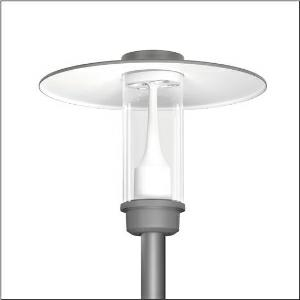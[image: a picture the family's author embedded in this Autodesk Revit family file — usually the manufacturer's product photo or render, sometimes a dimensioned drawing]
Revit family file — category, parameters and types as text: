
# Revit family: litepole_2_iq___p1_0a_5xa5425nf14hp_e36f
name_source: partatom
category: Lighting Fixtures
units: mm (PartAtom-declared; Revit-internal decimal feet)

## family parameters
Cut with Voids When Loaded = No
Host = Face
Light Source = No
Part Type = Normal
Room Calculation Point = No
Round Connector Dimension = Use Diameter
Shared = No

## types (1)
- --- (1 x LED, 4240 lm, 33.6 W, 2700K)
    Apparent Load = 34 VA
    CIE Flux Codes = 32 62 90 96 100
    Color Rendering = 70
    Color Temperature = 2700K
    Default Elevation = 1800 mm
    Description = Litepole 2 iQ, mast luminaire, Module 540 iQ-SR, primary light control with 3 zone facetted reflector, of plastic, silver coated, highly specular, structured, primary optical cover: cover, of PMMA, transparent, light distribution: P1.0a, light emission: direct distribution, primary light characteristic: strongly asymmetric, installation type: post-top, LED, High Power LED, rated luminous flux: 4.240lm, luminous efficacy: 126lm/W, light colour: 727, colour temperature: 2700K, control gear: iQ Street-Remote, control: pre-setting: logarithmic dimming characteristic, Street-Remote, Auto-Match, Temp-Guard, Lumen-Switch, Night-Set, Smart-Wire, Light-Fading, Desk-Remote (wireless, voltage-free reading and setting of iQ features in the workshop via application-optimized NFC function/RFID function), optimised constant luminous flux control (CLO 2.0), with terminal, 6-pole, max. 2.5mm², mains connection: 230..240V, AC, 50/60Hz, start of lifetime: 34W, end of service life: 36W, reduction: 15W, luminaire housing, upper part, of aluminium, coated, Siteco® metallic grey (DB 702S), diameter: 750mm, height: 590mm, spigot size: d x l = 76 x 70mm (post-top) | with reducer (optional accessory) 60 x 70mm, mounting height: 3..5m, post-top mast mounting element, of diecast aluminium, coated, Siteco® metallic grey (DB 702S), Module 540 iQ-SR, traffic white (RAL 9016), equipment: Power, protection rating (complete): IP65, insulation class (complete): insulation class II (safety insulation), certification: CE, ENEC, VDE, packaging unit: 1 piece

Light Distribution: P1.0a
    Height = 590 mm
    Lamp = 1 x LED
    Lamp Light Flux = 4240 lm
    Lamp Power = 33.6 W
    Lamp count = 1
    Length = 750 mm
    Luminous efficacy = 126 lm/W
    Manufacturer = Siteco
    ModVariant = No
    Model = 5XA5425NF14HP
    Number of Poles = 1
    OnlyDefault = Yes
    Power Factor = 1
    Product Name = Litepole 2 iQ | P1.0a
    Product group = mast luminaire | pylon top
    ProductGroupID = 6100
    Protection Class = Protection class II
    Protection Degree = IP 65
    RLX_Detail_Level = 1
    RLX_Emergency_Light_Flux = 0 lm
    RLX_Emergency_Type = 0
    RLX_Emergency_Type_DB = No
    RlxData = <blob elided: 32061 chars, md5=822b5c19>
    Socket = socket
    Standby Power = 0 W
    System Light Flux = 4240 lm
    System Power = 34 W
    Type Comments = factory setting: luminous flux: 100 % | dim-lin: 254 | 695 mA
    Type Image = l_1006518.jpg
    URL = http://relux.com
    VarID = @adj_152402
    Voltage = 0 V
    Weight = 0.00 kg
    Width = 0 mm  [stored 0 ft]

note: [stored X ft] marks values corroborated as IEEE doubles in the binary element streams (Revit-internal decimal feet)

## geometry (parser evidence)
native form markers: Blend x4, Sweep x11
no freeform markers — native parametric forms only
